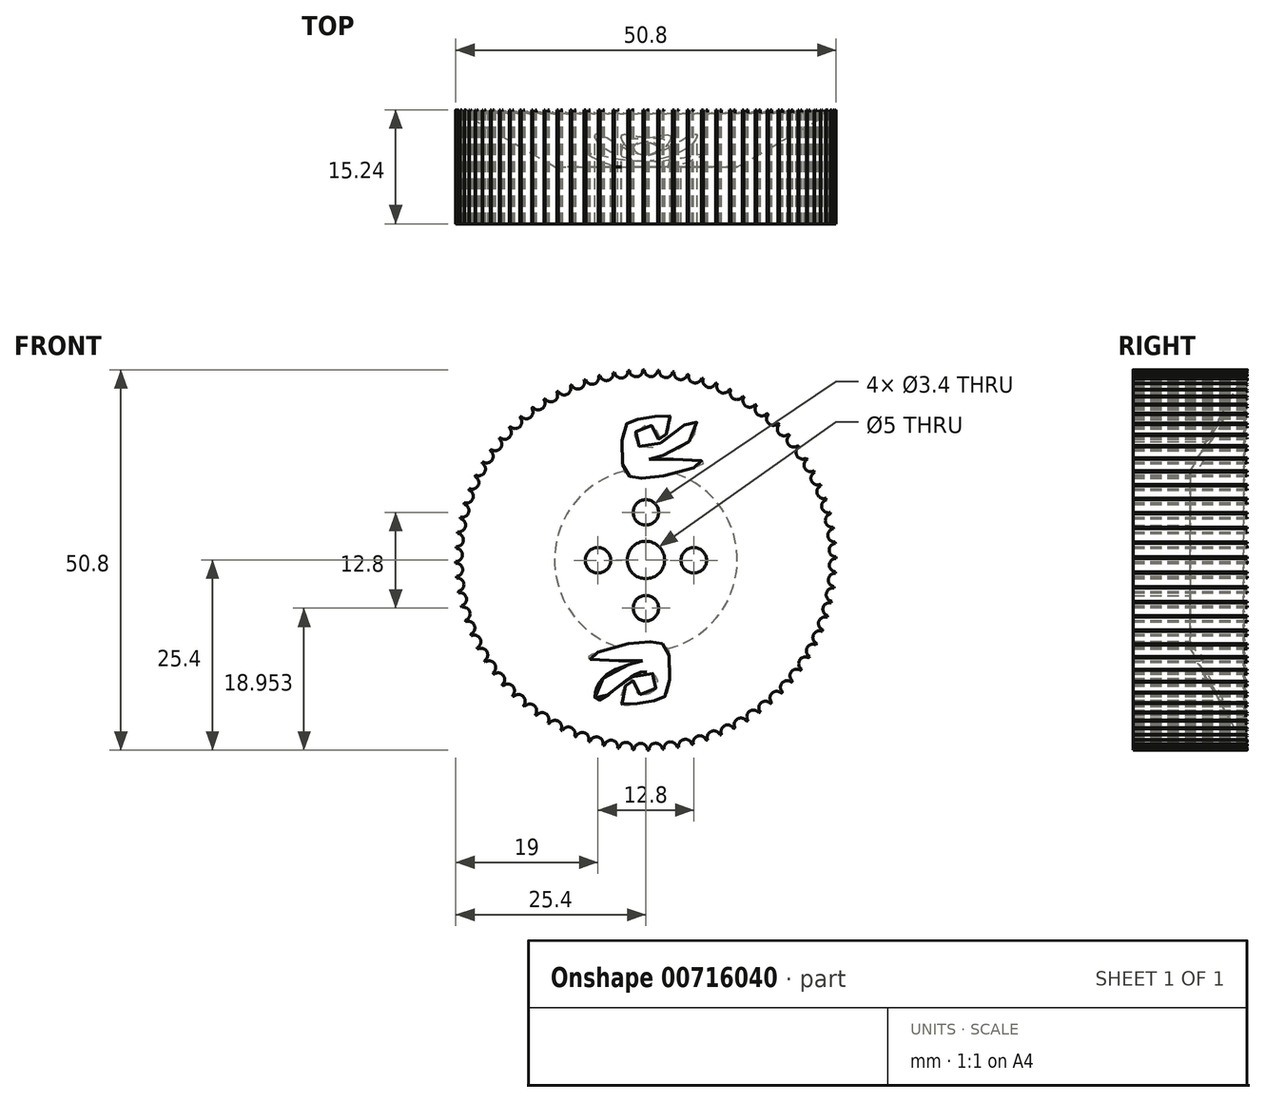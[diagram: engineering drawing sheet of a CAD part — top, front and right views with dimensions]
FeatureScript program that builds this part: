
annotation { "Feature Type Name" : "Feature", "Feature Type Description" : "" }
export const myFeature = defineFeature(function(context is Context, id is Id, definition is map)
    precondition{}
    {
        {
            var Q0;
            Q0=qCreatedBy(makeId("Front.planeOp"),FACE);
            var sketch = newSketch(context, id + "F0", { "sketchPlane" : qUnion([Q0])});
            skCircle(sketch, "E0", {"center": v(0, 0) * mm, "radius": 25.4 * mm});
            skCircle(sketch, "E1", {"center": v(0, 0) * mm, "radius": 2.5 * mm});
            skCircle(sketch, "E2", {"center": v(0, 6.35) * mm, "radius": 1.7 * mm});
            skCircle(sketch, "E3", {"center": v(6.4, -0.05) * mm, "radius": 1.7 * mm});
            skCircle(sketch, "E4", {"center": v(0, -6.45) * mm, "radius": 1.7 * mm});
            skCircle(sketch, "E5", {"center": v(-6.4, -0.05) * mm, "radius": 1.7 * mm});
            skSolve(sketch);
        }
        {
            var Q0;
            Q0=qSketchRegion(id+"F0",true);
            extrude(context, id + "F1", {"entities" : qUnion([Q0]), "depth" : 15.24 * mm, "offsetDistance" : 25.4 * mm});
        }
        {
            var Q0;
            Q0=makeQuery(id+"F0.imprint","IMPRINT",FACE,{"disambiguationData":[TD([[makeQuery(id+"F0.imprint","IMPRINT",EDGE,{"derivedFrom":sQuery(id+"F0.wireOp",EDGE,"E0")}),1.0]])]});
            var Q1;
            Q1=makeQuery(id+"F0.imprint","IMPRINT",FACE,{"disambiguationData":[TD([[makeQuery(id+"F0.imprint","IMPRINT",EDGE,{"derivedFrom":sQuery(id+"F0.wireOp",EDGE,"E5")}),1.0]])]});
            var Q2;
            Q2=makeQuery(id+"F0.imprint","IMPRINT",FACE,{"disambiguationData":[TD([[makeQuery(id+"F0.imprint","IMPRINT",EDGE,{"derivedFrom":sQuery(id+"F0.wireOp",EDGE,"E3")}),1.0]])]});
            var Q3;
            Q3=makeQuery(id+"F0.imprint","IMPRINT",FACE,{"disambiguationData":[TD([[makeQuery(id+"F0.imprint","IMPRINT",EDGE,{"derivedFrom":sQuery(id+"F0.wireOp",EDGE,"E2")}),1.0]])]});
            var Q4;
            Q4=makeQuery(id+"F0.imprint","IMPRINT",FACE,{"disambiguationData":[TD([[makeQuery(id+"F0.imprint","IMPRINT",EDGE,{"derivedFrom":sQuery(id+"F0.wireOp",EDGE,"E4")}),1.0]])]});
            var Q5;
            Q5=makeQuery(id+"F0.imprint","IMPRINT",FACE,{"disambiguationData":[TD([[makeQuery(id+"F0.imprint","IMPRINT",EDGE,{"derivedFrom":sQuery(id+"F0.wireOp",EDGE,"E1")}),1.0]])]});
            extrude(context, id + "F2", {"entities" : qUnion([Q0, Q1, Q2, Q3, Q4, Q5]), "operationType" : NewBodyOperationType.REMOVE, "depth" : 7.62 * mm, "offsetDistance" : 25.4 * mm, "hasDraft" : true, "draftAngle" : 60 * degree, "draftPullDirection" : true});
        }
        {
            var Q0;
            Q0=qCreatedBy(makeId("Front.planeOp"),FACE);
            var sketch = newSketch(context, id + "F3", { "sketchPlane" : qUnion([Q0])});
            skFitSpline(sketch, "E6", {"points": [v(0.43, 13.47) * mm, v(7.67, 13.14) * mm, v(1.54, 11.06) * mm, v(-1.72, 11.06) * mm, v(-2.9, 11.9) * mm, v(-2.9, 17.51) * mm, v(-1.91, 18.62) * mm, v(0.82, 19.08) * mm, v(3.3, 19.08) * mm, v(1.93, 15.82) * mm, v(1.09, 17.77) * mm, v(-1.52, 16.8) * mm, v(0.24, 14.9) * mm, v(6.5, 18.75) * mm, v(5.32, 15.43) * mm, v(0.43, 13.47) * mm]});
            skSolve(sketch);
        }
        {
            var Q0;
            Q0=qSketchRegion(id+"F3",true);
            extrude(context, id + "F4", {"entities" : qUnion([Q0]), "depth" : 25.4 * mm, "offsetDistance" : 25.4 * mm});
        }
        {
            var Q0;
            Q0=qCreatedBy(makeId("Top.planeOp"),FACE);
            var sketch = newSketch(context, id + "F5", { "sketchPlane" : qUnion([Q0])});
            skLineSegment(sketch, "E7", {"start": v(0, 35.49) * mm, "end": v(0, -33.64) * mm});
            skSolve(sketch);
        }
        {
            var Q0;
            Q0=makeQuery(id+"F4.opExtrude","SWEPT_BODY",BODY,{"disambiguationData":[OSD([sQuery(id+"F3.wireOp",EDGE,"E6")])]});
            var Q1;
            Q1=sQuery(id+"F5.wireOp",EDGE,"E7");
            circularPattern(context, id + "F6", {"operationType" : NewBodyOperationType.REMOVE, "entities" : qUnion([Q0]), "axis" : qUnion([Q1]), "angle" : 360 * degree, "instanceCount" : 2, "oppositeDirection" : true, "equalSpace" : true});
        }
        {
            var Q0;
            Q0=makeQuery(id+"F1.opExtrude","CAP_FACE",FACE,{"disambiguationData":[OSD([sQuery(id+"F0.wireOp",EDGE,"E0"),sQuery(id+"F0.wireOp",EDGE,"E1"),sQuery(id+"F0.wireOp",EDGE,"E2"),sQuery(id+"F0.wireOp",EDGE,"E3"),sQuery(id+"F0.wireOp",EDGE,"E4"),sQuery(id+"F0.wireOp",EDGE,"E5")])],"isStart":false});
            var sketch = newSketch(context, id + "F7", { "sketchPlane" : qUnion([Q0])});
            skCircle(sketch, "E8", {"center": v(-10.92, 22.93) * mm, "radius": 0.89 * mm});
            skSolve(sketch);
        }
        {
            var Q0;
            Q0=qSketchRegion(id+"F7",true);
            extrude(context, id + "F8", {"entities" : qUnion([Q0]), "endBound" : BoundingType.SYMMETRIC, "depth" : 50.8 * mm, "offsetDistance" : 25.4 * mm});
        }
        {
            var Q0;
            Q0=makeQuery(id+"F8.opExtrude","SWEPT_BODY",BODY,{"disambiguationData":[OSD([sQuery(id+"F7.wireOp",EDGE,"E8")])]});
            var Q1;
            Q1=sQuery(id+"F5.wireOp",EDGE,"E7");
            circularPattern(context, id + "F9", {"operationType" : NewBodyOperationType.REMOVE, "entities" : qUnion([Q0]), "axis" : qUnion([Q1]), "angle" : 360 * degree, "instanceCount" : 80, "equalSpace" : true});
        }
    });
